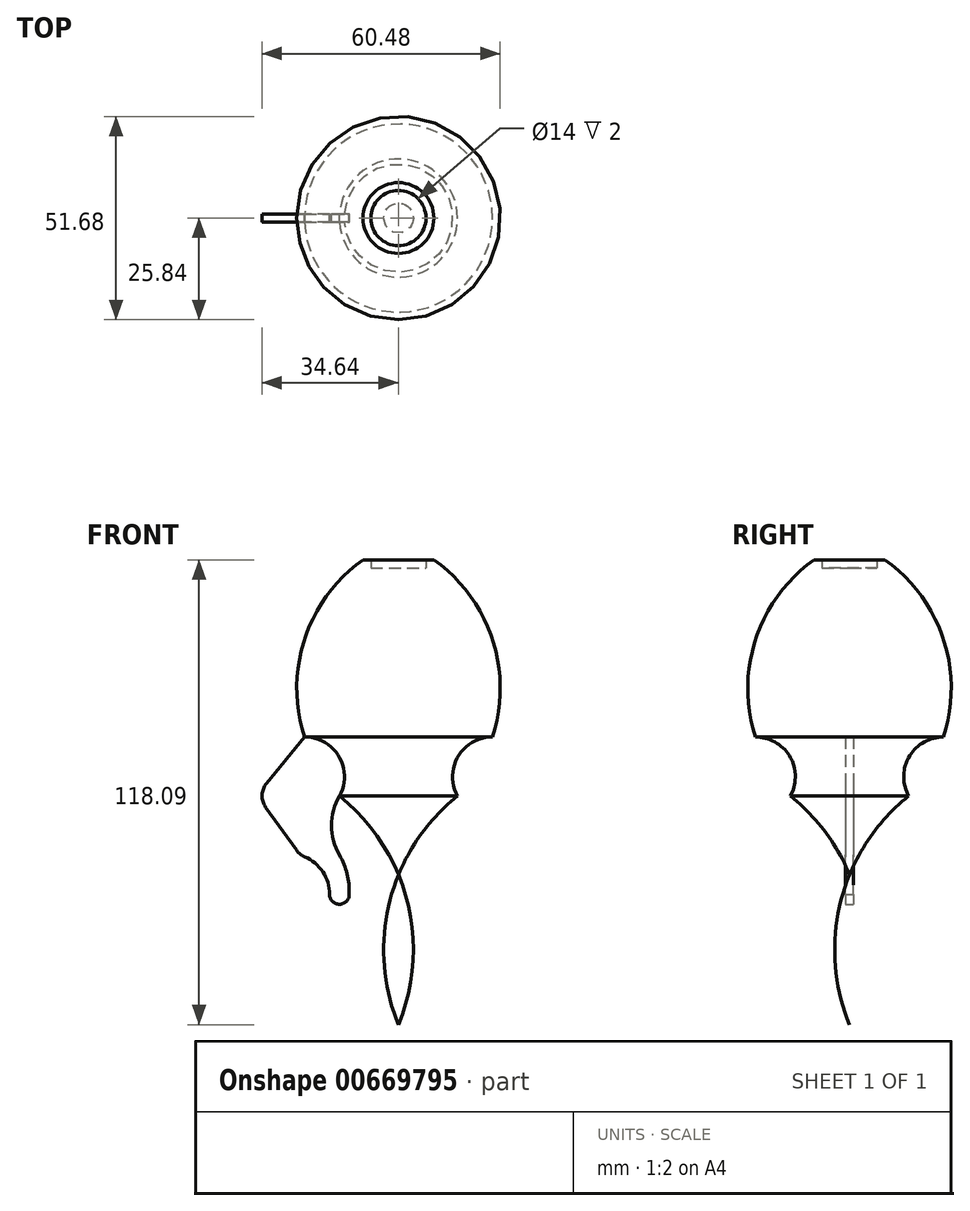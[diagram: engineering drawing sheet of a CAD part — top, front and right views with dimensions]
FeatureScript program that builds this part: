
annotation { "Feature Type Name" : "Feature", "Feature Type Description" : "" }
export const myFeature = defineFeature(function(context is Context, id is Id, definition is map)
    precondition{}
    {
        {
            var Q0;
            Q0=qCreatedBy(makeId("Front.planeOp"),FACE);
            var sketch = newSketch(context, id + "F0", { "sketchPlane" : qUnion([Q0])});
            skLineSegment(sketch, "E0", {"start": v(0, 0) * mm, "end": v(0, 80) * mm});
            skLineSegment(sketch, "E1", {"start": v(0, 80) * mm, "end": v(9, 80) * mm});
            skLineSegment(sketch, "E2", {"start": v(0, 35) * mm, "end": v(23.88, 35) * mm});
            skLineSegment(sketch, "E3", {"start": v(0, 20) * mm, "end": v(15, 20) * mm});
            skArc(sketch, "E4", {"start": v(23.88, 35) * mm, "mid": v(23.82, 59.94) * mm, "end": v(9, 80) * mm});
            skArc(sketch, "E5", {"start": v(15, 20) * mm, "mid": v(6.23, 10.95) * mm, "end": v(0, 0) * mm});
            skLineSegment(sketch, "E6", {"start": v(0, 78) * mm, "end": v(7, 78) * mm});
            skLineSegment(sketch, "E7", {"start": v(7, 80) * mm, "end": v(7, 78) * mm});
            skArc(sketch, "E8", {"start": v(23.88, 35) * mm, "mid": v(15.16, 30.03) * mm, "end": v(15, 20) * mm});
            skSolve(sketch);
        }
        {
            var Q0;
            {var subQ2=sQuery(id+"F0.wireOp",EDGE,"E3");Q0=makeQuery(id+"F0.imprint","IMPRINT",FACE,{"disambiguationData":[TD([[makeQuery(id+"F0.imprint","IMPRINT",EDGE,{"derivedFrom":subQ2}),-1.0]])]});}
            var Q1;
            {var subQ0=sQuery(id+"F0.wireOp",EDGE,"E2");Q1=makeQuery(id+"F0.imprint","IMPRINT",FACE,{"disambiguationData":[TD([[makeQuery(id+"F0.imprint","IMPRINT",EDGE,{"derivedFrom":subQ0}),-1.0]])]});}
            var Q2;
            {var subQ1=sQuery(id+"F0.wireOp",EDGE,"E2");Q2=makeQuery(id+"F0.imprint","IMPRINT",FACE,{"disambiguationData":[TD([[makeQuery(id+"F0.imprint","IMPRINT",EDGE,{"derivedFrom":subQ1}),1.0]])]});}
            var Q3;
            Q3=sQuery(id+"F0.wireOp",EDGE,"E0");
            revolve(context, id + "F1", {"entities" : qUnion([Q0, Q1, Q2]), "axis" : qUnion([Q3]), "revolveType" : RevolveType.FULL});
        }
        {
            var Q0;
            Q0=qCreatedBy(makeId("Front.planeOp"),FACE);
            var sketch = newSketch(context, id + "F2", { "sketchPlane" : qUnion([Q0])});
            skLineSegment(sketch, "E9.0", {"start": v(23.88, 35) * mm, "end": v(-23.88, 35) * mm});
            skLineSegment(sketch, "E10.0", {"start": v(15, 20) * mm, "end": v(-15, 20) * mm});
            skArc(sketch, "E11", {"start": v(-15, 20) * mm, "mid": v(-15.16, 30.03) * mm, "end": v(-23.88, 35) * mm});
            skLineSegment(sketch, "E12", {"start": v(-23.88, 35) * mm, "end": v(-15, 20) * mm});
            skLineSegment(sketch, "E13", {"start": v(0, 20) * mm, "end": v(0, 35) * mm});
            skSolve(sketch);
        }
        {
            var Q0;
            Q0=makeQuery(id+"F2.imprint","IMPRINT",FACE,{"disambiguationData":[TD([[makeQuery(id+"F2.imprint","IMPRINT",EDGE,{"derivedFrom":sQuery(id+"F2.wireOp",EDGE,"E11")}),1.0]])]});
            var Q1;
            {var subQ1=sQuery(id+"F2.wireOp",EDGE,"E11");Q1=makeQuery(id+"F2.imprint","IMPRINT",FACE,{"disambiguationData":[TD([[makeQuery(id+"F2.imprint","IMPRINT",EDGE,{"derivedFrom":subQ1}),-1.0]])]});}
            extrude(context, id + "F3", {"entities" : qUnion([Q0, Q1]), "operationType" : NewBodyOperationType.ADD, "depth" : 2 * mm, "offsetDistance" : 25 * mm, "symmetric" : true});
        }
        {
            var Q0;
            Q0=qCreatedBy(makeId("Front.planeOp"),FACE);
            var sketch = newSketch(context, id + "F4", { "sketchPlane" : qUnion([Q0])});
            skLineSegment(sketch, "E14", {"start": v(0, 0) * mm, "end": v(0, -5) * mm});
            skLineSegment(sketch, "E15", {"start": v(0, -5) * mm, "end": v(-15, -5) * mm});
            skLineSegment(sketch, "E16", {"start": v(-15, -5) * mm, "end": v(-15, 5) * mm});
            skLineSegment(sketch, "E17", {"start": v(-15, 5) * mm, "end": v(-25, 5) * mm});
            skArc(sketch, "E18", {"start": v(-17.5, -5) * mm, "mid": v(-15, -7.5) * mm, "end": v(-12.5, -5) * mm});
            skLineSegment(sketch, "E19", {"start": v(-15, -5) * mm, "end": v(-17.5, -5) * mm});
            skArc(sketch, "E20", {"start": v(-12.5, -5) * mm, "mid": v(-13.05, 0.17) * mm, "end": v(-15, 5) * mm});
            skArc(sketch, "E21", {"start": v(-17.5, -5) * mm, "mid": v(-19.22, 0.73) * mm, "end": v(-23.8, 4.57) * mm});
            skLineSegment(sketch, "E22.0", {"start": v(-23.86, 35) * mm, "end": v(23.88, 35) * mm});
            skLineSegment(sketch, "E23", {"start": v(-23.86, 35) * mm, "end": v(-33.5, 23.24) * mm});
            skLineSegment(sketch, "E24", {"start": v(-33.7, 17.16) * mm, "end": v(-25.9, 6.25) * mm});
            skLineSegment(sketch, "E25.0", {"start": v(-14.97, 20) * mm, "end": v(15, 20) * mm});
            skArc(sketch, "E26", {"start": v(-14.97, 20) * mm, "mid": v(-17, 12.5) * mm, "end": v(-15, 5) * mm});
            skFitSpline(sketch, "E27.0", {"points": [v(-23.86, 35) * mm, v(-23.42, 35) * mm, v(-22.77, 34.96) * mm, v(-21.9, 34.82) * mm, v(-21.04, 34.62) * mm, v(-20.22, 34.34) * mm, v(-19.42, 33.99) * mm, v(-18.64, 33.57) * mm, v(-17.73, 32.98) * mm, v(-16.9, 32.26) * mm, v(-16.3, 31.63) * mm, v(-15.73, 30.96) * mm, v(-15.24, 30.24) * mm, v(-14.81, 29.47) * mm, v(-14.44, 28.67) * mm, v(-14.07, 27.64) * mm, v(-13.8, 26.37) * mm, v(-13.69, 25.04) * mm, v(-13.74, 23.95) * mm, v(-13.87, 23.07) * mm, v(-14.05, 22.22) * mm, v(-14.32, 21.4) * mm, v(-14.66, 20.59) * mm, v(-14.86, 20.2) * mm, v(-14.97, 20) * mm]});
            skPoint(sketch, "E28.visualSharp", {"position": v(-35.94, 20.27) * mm});
            skArc(sketch, "E28.filletArc", {"start": v(-33.5, 23.24) * mm, "mid": v(-34.64, 20.23) * mm, "end": v(-33.7, 17.16) * mm});
            skPoint(sketch, "E29.visualSharp", {"position": v(-25, 5) * mm});
            skArc(sketch, "E29.filletArc", {"start": v(-25.9, 6.25) * mm, "mid": v(-24.97, 5.27) * mm, "end": v(-23.8, 4.57) * mm});
            skSolve(sketch);
        }
        {
            var Q0;
            Q0=makeQuery(id+"F4.imprint","IMPRINT",FACE,{"disambiguationData":[TD([[makeQuery(id+"F4.imprint","IMPRINT",EDGE,{"derivedFrom":sQuery(id+"F4.wireOp",EDGE,"E23")}),1.0]])]});
            var Q1;
            {var subQ1=sQuery(id+"F4.wireOp",EDGE,"E16");Q1=makeQuery(id+"F4.imprint","IMPRINT",FACE,{"disambiguationData":[TD([[makeQuery(id+"F4.imprint","IMPRINT",EDGE,{"derivedFrom":subQ1}),1.0]])]});}
            var Q2;
            {var subQ2=sQuery(id+"F4.wireOp",EDGE,"E18");Q2=makeQuery(id+"F4.imprint","IMPRINT",FACE,{"disambiguationData":[TD([[makeQuery(id+"F4.imprint","IMPRINT",EDGE,{"derivedFrom":subQ2}),1.0]])]});}
            var Q3;
            {var subQ0=sQuery(id+"F4.wireOp",EDGE,"E16");Q3=makeQuery(id+"F4.imprint","IMPRINT",FACE,{"disambiguationData":[TD([[makeQuery(id+"F4.imprint","IMPRINT",EDGE,{"derivedFrom":subQ0}),-1.0]])]});}
            extrude(context, id + "F5", {"entities" : qUnion([Q0, Q1, Q2, Q3]), "operationType" : NewBodyOperationType.ADD, "depth" : 2 * mm, "offsetDistance" : 25 * mm, "symmetric" : true});
        }
    });
